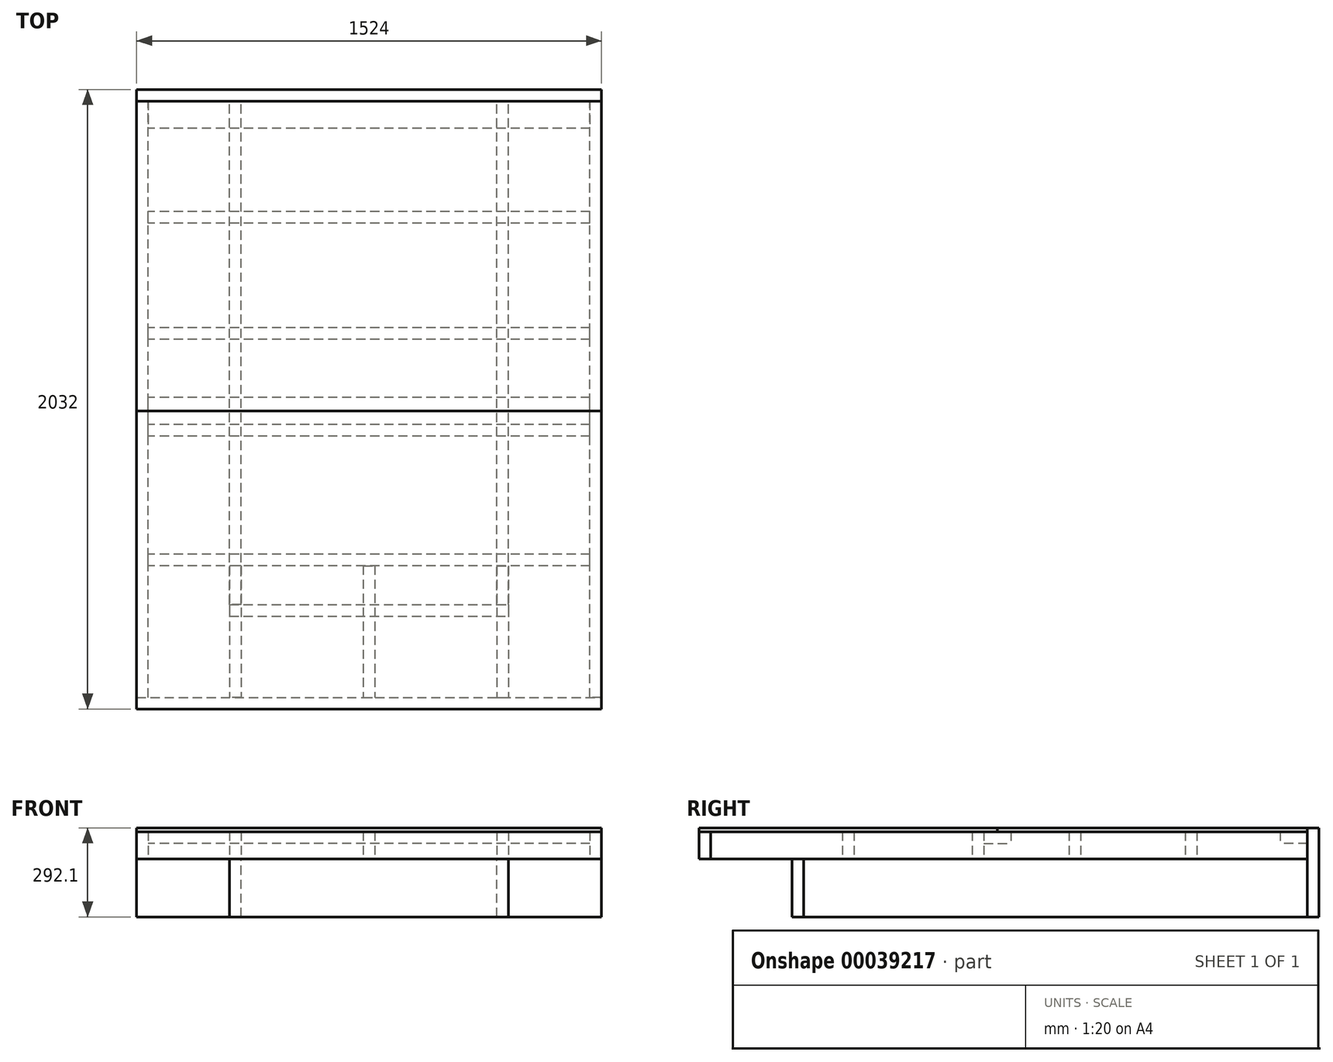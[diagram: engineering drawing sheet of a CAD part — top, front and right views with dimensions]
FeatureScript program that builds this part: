
annotation { "Feature Type Name" : "Feature", "Feature Type Description" : "" }
export const myFeature = defineFeature(function(context is Context, id is Id, definition is map)
    precondition{}
    {
        {
            var Q0;
            Q0=qCreatedBy(makeId("Front.planeOp"),FACE);
            var sketch = newSketch(context, id + "F0", { "sketchPlane" : qUnion([Q0])});
            skLineSegment(sketch, "E0.bottom", {"start": v(-762, 0) * mm, "end": v(762, 0) * mm});
            skLineSegment(sketch, "E0.top", {"start": v(-762, 292.1) * mm, "end": v(762, 292.1) * mm});
            skLineSegment(sketch, "E0.left", {"start": v(-762, 0) * mm, "end": v(-762, 292.1) * mm});
            skLineSegment(sketch, "E0.right", {"start": v(762, 0) * mm, "end": v(762, 292.1) * mm});
            skSolve(sketch);
        }
        {
            var Q0;
            Q0=makeQuery(id+"F0.imprint","IMPRINT",FACE,{"disambiguationData":[TD([[makeQuery(id+"F0.imprint","IMPRINT",EDGE,{"derivedFrom":sQuery(id+"F0.wireOp",EDGE,"E0.bottom")}),1.0]])]});
            extrude(context, id + "F1", {"entities" : qUnion([Q0]), "depth" : 38.1 * mm});
        }
        {
            var Q0;
            Q0=makeQuery(id+"F1.opExtrude","CAP_FACE",FACE,{"disambiguationData":[OSD([sQuery(id+"F0.wireOp",EDGE,"E0.bottom"),sQuery(id+"F0.wireOp",EDGE,"E0.top"),sQuery(id+"F0.wireOp",EDGE,"E0.left"),sQuery(id+"F0.wireOp",EDGE,"E0.right")])],"isStart":false});
            var sketch = newSketch(context, id + "F2", { "sketchPlane" : qUnion([Q0])});
            skLineSegment(sketch, "E1.bottom", {"start": v(419.1, 0) * mm, "end": v(457.2, 0) * mm});
            skLineSegment(sketch, "E1.top", {"start": v(419.1, 190.5) * mm, "end": v(457.2, 190.5) * mm});
            skLineSegment(sketch, "E1.left", {"start": v(419.1, 0) * mm, "end": v(419.1, 190.5) * mm});
            skLineSegment(sketch, "E1.right", {"start": v(457.2, 0) * mm, "end": v(457.2, 190.5) * mm});
            skSolve(sketch);
        }
        {
            var Q0;
            Q0=makeQuery(id+"F2.imprint","IMPRINT",FACE,{"disambiguationData":[TD([[makeQuery(id+"F2.imprint","IMPRINT",EDGE,{"derivedFrom":sQuery(id+"F2.wireOp",EDGE,"E1.bottom")}),1.0]])]});
            extrude(context, id + "F3", {"entities" : qUnion([Q0]), "depth" : 1651 * mm});
        }
        {
            var Q0;
            Q0=makeQuery(id+"F3.opExtrude","SWEPT_BODY",BODY,{"disambiguationData":[OSD([sQuery(id+"F2.wireOp",EDGE,"E1.bottom"),sQuery(id+"F2.wireOp",EDGE,"E1.top"),sQuery(id+"F2.wireOp",EDGE,"E1.left"),sQuery(id+"F2.wireOp",EDGE,"E1.right")])]});
            var Q1;
            Q1=qCreatedBy(makeId("Right.planeOp"),FACE);
            mirror(context, id + "F4", {"entities" : qUnion([Q0]), "mirrorPlane" : qUnion([Q1])});
        }
        {
            var Q0;
            Q0=makeQuery(id+"F3.opExtrude","SWEPT_FACE",FACE,{"disambiguationData":[OSD([sQuery(id+"F2.wireOp",EDGE,"E1.right")])]});
            var sketch = newSketch(context, id + "F5", { "sketchPlane" : qUnion([Q0])});
            skLineSegment(sketch, "E2.bottom", {"start": v(-1689.1, 190.5) * mm, "end": v(-1727.2, 190.5) * mm});
            skLineSegment(sketch, "E2.top", {"start": v(-1689.1, 0) * mm, "end": v(-1727.2, 0) * mm});
            skLineSegment(sketch, "E2.left", {"start": v(-1689.1, 190.5) * mm, "end": v(-1689.1, 0) * mm});
            skLineSegment(sketch, "E2.right", {"start": v(-1727.2, 190.5) * mm, "end": v(-1727.2, 0) * mm});
            skSolve(sketch);
        }
        {
            var Q0;
            Q0=makeQuery(id+"F5.imprint","IMPRINT",FACE,{"disambiguationData":[TD([[makeQuery(id+"F5.imprint","IMPRINT",EDGE,{"derivedFrom":sQuery(id+"F5.wireOp",EDGE,"E2.bottom")}),1.0]])]});
            extrude(context, id + "F6", {"entities" : qUnion([Q0]), "oppositeDirection" : true, "depth" : 914.4 * mm});
        }
        {
            var Q0;
            Q0=makeQuery(id+"F1.opExtrude","CAP_FACE",FACE,{"disambiguationData":[OSD([sQuery(id+"F0.wireOp",EDGE,"E0.bottom"),sQuery(id+"F0.wireOp",EDGE,"E0.top"),sQuery(id+"F0.wireOp",EDGE,"E0.left"),sQuery(id+"F0.wireOp",EDGE,"E0.right")])],"isStart":false});
            var sketch = newSketch(context, id + "F7", { "sketchPlane" : qUnion([Q0])});
            skLineSegment(sketch, "E3.bottom", {"start": v(-762, 279.4) * mm, "end": v(-723.9, 279.4) * mm});
            skLineSegment(sketch, "E3.top", {"start": v(-762, 190.5) * mm, "end": v(-723.9, 190.5) * mm});
            skLineSegment(sketch, "E3.left", {"start": v(-762, 279.4) * mm, "end": v(-762, 190.5) * mm});
            skLineSegment(sketch, "E3.right", {"start": v(-723.9, 279.4) * mm, "end": v(-723.9, 190.5) * mm});
            skSolve(sketch);
        }
        {
            var Q0;
            Q0=makeQuery(id+"F7.imprint","IMPRINT",FACE,{"disambiguationData":[TD([[makeQuery(id+"F7.imprint","IMPRINT",EDGE,{"derivedFrom":sQuery(id+"F7.wireOp",EDGE,"E3.bottom")}),-1.0]])]});
            extrude(context, id + "F8", {"entities" : qUnion([Q0]), "depth" : 1955.8 * mm});
        }
        {
            var Q0;
            Q0=makeQuery(id+"F8.opExtrude","SWEPT_BODY",BODY,{"disambiguationData":[OSD([sQuery(id+"F7.wireOp",EDGE,"E3.bottom"),sQuery(id+"F7.wireOp",EDGE,"E3.top"),sQuery(id+"F7.wireOp",EDGE,"E3.left"),sQuery(id+"F7.wireOp",EDGE,"E3.right")])]});
            var Q1;
            Q1=qCreatedBy(makeId("Right.planeOp"),FACE);
            mirror(context, id + "F9", {"entities" : qUnion([Q0]), "mirrorPlane" : qUnion([Q1])});
        }
        {
            var Q0;
            Q0=makeQuery(id+"F9.opPattern","COPY",FACE,{"derivedFrom":makeQuery(id+"F8.opExtrude","SWEPT_FACE",FACE,{"disambiguationData":[OSD([sQuery(id+"F7.wireOp",EDGE,"E3.left")])]}),"instanceName":"1"});
            var sketch = newSketch(context, id + "F10", { "sketchPlane" : qUnion([Q0])});
            skLineSegment(sketch, "E4.bottom", {"start": v(-1993.9, 279.4) * mm, "end": v(-2032, 279.4) * mm});
            skLineSegment(sketch, "E4.top", {"start": v(-1993.9, 190.5) * mm, "end": v(-2032, 190.5) * mm});
            skLineSegment(sketch, "E4.left", {"start": v(-1993.9, 279.4) * mm, "end": v(-1993.9, 190.5) * mm});
            skLineSegment(sketch, "E4.right", {"start": v(-2032, 279.4) * mm, "end": v(-2032, 190.5) * mm});
            skSolve(sketch);
        }
        {
            var Q0;
            Q0 = qSketchRegion(id + "F10", true);
            extrude(context, id + "F11", {"entities" : qUnion([Q0]), "oppositeDirection" : true, "depth" : 1524 * mm});
        }
        {
            var Q0;
            Q0=makeQuery(id+"F11.opExtrude","SWEPT_FACE",FACE,{"disambiguationData":[OSD([sQuery(id+"F10.wireOp",EDGE,"E4.left")])]});
            var sketch = newSketch(context, id + "F12", { "sketchPlane" : qUnion([Q0])});
            skLineSegment(sketch, "E5.bottom", {"start": v(-457.2, 279.4) * mm, "end": v(-419.1, 279.4) * mm});
            skLineSegment(sketch, "E5.top", {"start": v(-457.2, 190.5) * mm, "end": v(-419.1, 190.5) * mm});
            skLineSegment(sketch, "E5.left", {"start": v(-457.2, 279.4) * mm, "end": v(-457.2, 190.5) * mm});
            skLineSegment(sketch, "E5.right", {"start": v(-419.1, 279.4) * mm, "end": v(-419.1, 190.5) * mm});
            skSolve(sketch);
        }
        {
            var Q0;
            Q0=makeQuery(id+"F12.imprint","IMPRINT",FACE,{"disambiguationData":[TD([[makeQuery(id+"F12.imprint","IMPRINT",EDGE,{"derivedFrom":sQuery(id+"F12.wireOp",EDGE,"E5.bottom")}),1.0]])]});
            extrude(context, id + "F13", {"entities" : qUnion([Q0]), "depth" : 431.8 * mm});
        }
        {
            var Q0;
            Q0=makeQuery(id+"F13.opExtrude","SWEPT_BODY",BODY,{"disambiguationData":[OSD([sQuery(id+"F12.wireOp",EDGE,"E5.bottom"),sQuery(id+"F12.wireOp",EDGE,"E5.top"),sQuery(id+"F12.wireOp",EDGE,"E5.left"),sQuery(id+"F12.wireOp",EDGE,"E5.right")])]});
            var Q1;
            Q1=qCreatedBy(makeId("Right.planeOp"),FACE);
            mirror(context, id + "F14", {"entities" : qUnion([Q0]), "mirrorPlane" : qUnion([Q1])});
        }
        {
            var Q0;
            Q0=makeQuery(id+"F11.opExtrude","SWEPT_FACE",FACE,{"disambiguationData":[OSD([sQuery(id+"F10.wireOp",EDGE,"E4.left")])]});
            var sketch = newSketch(context, id + "F15", { "sketchPlane" : qUnion([Q0])});
            skLineSegment(sketch, "E6.bottom", {"start": v(-19.05, 279.4) * mm, "end": v(19.05, 279.4) * mm});
            skLineSegment(sketch, "E6.top", {"start": v(-19.05, 190.5) * mm, "end": v(19.05, 190.5) * mm});
            skLineSegment(sketch, "E6.left", {"start": v(-19.05, 279.4) * mm, "end": v(-19.05, 190.5) * mm});
            skLineSegment(sketch, "E6.right", {"start": v(19.05, 279.4) * mm, "end": v(19.05, 190.5) * mm});
            skSolve(sketch);
        }
        {
            var Q0;
            Q0=makeQuery(id+"F15.imprint","IMPRINT",FACE,{"disambiguationData":[TD([[makeQuery(id+"F15.imprint","IMPRINT",EDGE,{"derivedFrom":sQuery(id+"F15.wireOp",EDGE,"E6.bottom")}),1.0]])]});
            extrude(context, id + "F16", {"entities" : qUnion([Q0]), "depth" : 431.8 * mm});
        }
        {
            var Q0;
            Q0=makeQuery(id+"F8.opExtrude","SWEPT_FACE",FACE,{"disambiguationData":[OSD([sQuery(id+"F7.wireOp",EDGE,"E3.right")])]});
            var sketch = newSketch(context, id + "F17", { "sketchPlane" : qUnion([Q0])});
            skLineSegment(sketch, "E7.bottom", {"start": v(-1524, 279.4) * mm, "end": v(-1562.1, 279.4) * mm});
            skLineSegment(sketch, "E7.top", {"start": v(-1524, 190.5) * mm, "end": v(-1562.1, 190.5) * mm});
            skLineSegment(sketch, "E7.left", {"start": v(-1524, 279.4) * mm, "end": v(-1524, 190.5) * mm});
            skLineSegment(sketch, "E7.right", {"start": v(-1562.1, 279.4) * mm, "end": v(-1562.1, 190.5) * mm});
            skSolve(sketch);
        }
        {
            var Q0;
            Q0=makeQuery(id+"F17.imprint","IMPRINT",FACE,{"disambiguationData":[TD([[makeQuery(id+"F17.imprint","IMPRINT",EDGE,{"derivedFrom":sQuery(id+"F17.wireOp",EDGE,"E7.bottom")}),-1.0]])]});
            extrude(context, id + "F18", {"entities" : qUnion([Q0]), "depth" : 1447.8 * mm});
        }
        {
            var Q0;
            Q0=makeQuery(id+"F8.opExtrude","SWEPT_FACE",FACE,{"disambiguationData":[OSD([sQuery(id+"F7.wireOp",EDGE,"E3.right")])]});
            var sketch = newSketch(context, id + "F19", { "sketchPlane" : qUnion([Q0])});
            skLineSegment(sketch, "E8.bottom", {"start": v(-1098.55, 279.4) * mm, "end": v(-1009.65, 279.4) * mm});
            skLineSegment(sketch, "E8.top", {"start": v(-1098.55, 241.3) * mm, "end": v(-1009.65, 241.3) * mm});
            skLineSegment(sketch, "E8.left", {"start": v(-1098.55, 279.4) * mm, "end": v(-1098.55, 241.3) * mm});
            skLineSegment(sketch, "E8.right", {"start": v(-1009.65, 279.4) * mm, "end": v(-1009.65, 241.3) * mm});
            skSolve(sketch);
        }
        {
            var Q0;
            Q0=makeQuery(id+"F19.imprint","IMPRINT",FACE,{"disambiguationData":[TD([[makeQuery(id+"F19.imprint","IMPRINT",EDGE,{"derivedFrom":sQuery(id+"F19.wireOp",EDGE,"E8.bottom")}),-1.0]])]});
            extrude(context, id + "F20", {"entities" : qUnion([Q0]), "depth" : 1447.8 * mm});
        }
        {
            var Q0;
            Q0=makeQuery(id+"F8.opExtrude","SWEPT_FACE",FACE,{"disambiguationData":[OSD([sQuery(id+"F7.wireOp",EDGE,"E3.right")])]});
            var sketch = newSketch(context, id + "F21", { "sketchPlane" : qUnion([Q0])});
            skLineSegment(sketch, "E9.bottom", {"start": v(-1136.65, 279.4) * mm, "end": v(-1098.55, 279.4) * mm});
            skLineSegment(sketch, "E9.top", {"start": v(-1136.65, 190.5) * mm, "end": v(-1098.55, 190.5) * mm});
            skLineSegment(sketch, "E9.left", {"start": v(-1136.65, 279.4) * mm, "end": v(-1136.65, 190.5) * mm});
            skLineSegment(sketch, "E9.right", {"start": v(-1098.55, 279.4) * mm, "end": v(-1098.55, 190.5) * mm});
            skSolve(sketch);
        }
        {
            var Q0;
            Q0=makeQuery(id+"F21.imprint","IMPRINT",FACE,{"disambiguationData":[TD([[makeQuery(id+"F21.imprint","IMPRINT",EDGE,{"derivedFrom":sQuery(id+"F21.wireOp",EDGE,"E9.bottom")}),-1.0]])]});
            extrude(context, id + "F22", {"entities" : qUnion([Q0]), "depth" : 1447.8 * mm});
        }
        {
            var Q0;
            Q0=makeQuery(id+"F8.opExtrude","SWEPT_FACE",FACE,{"disambiguationData":[OSD([sQuery(id+"F7.wireOp",EDGE,"E3.right")])]});
            var sketch = newSketch(context, id + "F23", { "sketchPlane" : qUnion([Q0])});
            skLineSegment(sketch, "E10.bottom", {"start": v(-38.1, 279.4) * mm, "end": v(-127, 279.4) * mm});
            skLineSegment(sketch, "E10.top", {"start": v(-38.1, 241.3) * mm, "end": v(-127, 241.3) * mm});
            skLineSegment(sketch, "E10.left", {"start": v(-38.1, 279.4) * mm, "end": v(-38.1, 241.3) * mm});
            skLineSegment(sketch, "E10.right", {"start": v(-127, 279.4) * mm, "end": v(-127, 241.3) * mm});
            skSolve(sketch);
        }
        {
            var Q0;
            Q0=makeQuery(id+"F23.imprint","IMPRINT",FACE,{"disambiguationData":[TD([[makeQuery(id+"F23.imprint","IMPRINT",EDGE,{"derivedFrom":sQuery(id+"F23.wireOp",EDGE,"E10.bottom")}),-1.0]])]});
            extrude(context, id + "F24", {"entities" : qUnion([Q0]), "depth" : 1447.8 * mm});
        }
        {
            var Q0;
            Q0=makeQuery(id+"F8.opExtrude","SWEPT_FACE",FACE,{"disambiguationData":[OSD([sQuery(id+"F7.wireOp",EDGE,"E3.right")])]});
            var sketch = newSketch(context, id + "F25", { "sketchPlane" : qUnion([Q0])});
            skLineSegment(sketch, "E11.bottom", {"start": v(-819.15, 279.4) * mm, "end": v(-781.05, 279.4) * mm});
            skLineSegment(sketch, "E11.top", {"start": v(-819.15, 190.5) * mm, "end": v(-781.05, 190.5) * mm});
            skLineSegment(sketch, "E11.left", {"start": v(-819.15, 279.4) * mm, "end": v(-819.15, 190.5) * mm});
            skLineSegment(sketch, "E11.right", {"start": v(-781.05, 279.4) * mm, "end": v(-781.05, 190.5) * mm});
            skSolve(sketch);
        }
        {
            var Q0;
            Q0=makeQuery(id+"F25.imprint","IMPRINT",FACE,{"disambiguationData":[TD([[makeQuery(id+"F25.imprint","IMPRINT",EDGE,{"derivedFrom":sQuery(id+"F25.wireOp",EDGE,"E11.bottom")}),-1.0]])]});
            extrude(context, id + "F26", {"entities" : qUnion([Q0]), "depth" : 1447.8 * mm});
        }
        {
            var Q0;
            Q0=makeQuery(id+"F8.opExtrude","SWEPT_FACE",FACE,{"disambiguationData":[OSD([sQuery(id+"F7.wireOp",EDGE,"E3.right")])]});
            var sketch = newSketch(context, id + "F27", { "sketchPlane" : qUnion([Q0])});
            skLineSegment(sketch, "E12.bottom", {"start": v(-438.15, 279.4) * mm, "end": v(-400.05, 279.4) * mm});
            skLineSegment(sketch, "E12.top", {"start": v(-438.15, 190.5) * mm, "end": v(-400.05, 190.5) * mm});
            skLineSegment(sketch, "E12.left", {"start": v(-438.15, 279.4) * mm, "end": v(-438.15, 190.5) * mm});
            skLineSegment(sketch, "E12.right", {"start": v(-400.05, 279.4) * mm, "end": v(-400.05, 190.5) * mm});
            skSolve(sketch);
        }
        {
            var Q0;
            Q0 = qSketchRegion(id + "F27", true);
            extrude(context, id + "F28", {"entities" : qUnion([Q0]), "depth" : 1447.8 * mm});
        }
        {
            var Q0;
            Q0=makeQuery(id+"F11.opExtrude","SWEPT_FACE",FACE,{"disambiguationData":[OSD([sQuery(id+"F10.wireOp",EDGE,"E4.bottom")])]});
            var sketch = newSketch(context, id + "F29", { "sketchPlane" : qUnion([Q0])});
            skLineSegment(sketch, "E13.bottom", {"start": v(-762, -2032) * mm, "end": v(762, -2032) * mm});
            skLineSegment(sketch, "E13.top", {"start": v(-762, -1054.1) * mm, "end": v(762, -1054.1) * mm});
            skLineSegment(sketch, "E13.left", {"start": v(-762, -2032) * mm, "end": v(-762, -1054.1) * mm});
            skLineSegment(sketch, "E13.right", {"start": v(762, -2032) * mm, "end": v(762, -1054.1) * mm});
            skSolve(sketch);
        }
        {
            var Q0;
            Q0 = qSketchRegion(id + "F29", true);
            extrude(context, id + "F30", {"entities" : qUnion([Q0]), "depth" : 12.7 * mm});
        }
        {
            var Q0;
            Q0=makeQuery(id+"F8.opExtrude","SWEPT_FACE",FACE,{"disambiguationData":[OSD([sQuery(id+"F7.wireOp",EDGE,"E3.bottom")])]});
            var sketch = newSketch(context, id + "F31", { "sketchPlane" : qUnion([Q0])});
            skLineSegment(sketch, "E14.bottom", {"start": v(-762, -38.1) * mm, "end": v(762, -38.1) * mm});
            skLineSegment(sketch, "E14.top", {"start": v(-762, -1054.1) * mm, "end": v(762, -1054.1) * mm});
            skLineSegment(sketch, "E14.left", {"start": v(-762, -38.1) * mm, "end": v(-762, -1054.1) * mm});
            skLineSegment(sketch, "E14.right", {"start": v(762, -38.1) * mm, "end": v(762, -1054.1) * mm});
            skSolve(sketch);
        }
        {
            var Q0;
            Q0 = qSketchRegion(id + "F31", true);
            extrude(context, id + "F32", {"entities" : qUnion([Q0]), "depth" : 12.7 * mm});
        }
    });
